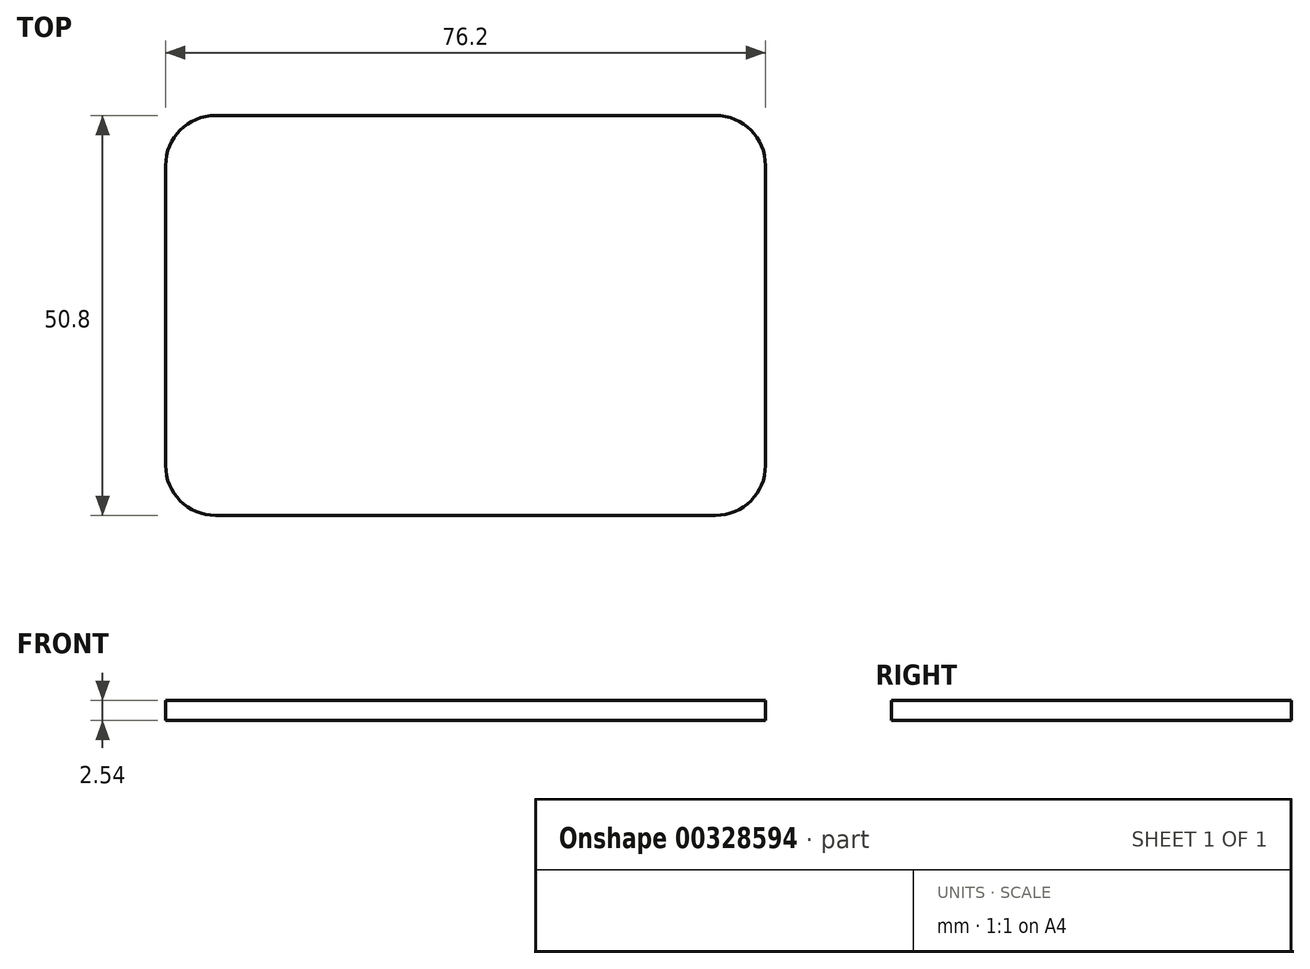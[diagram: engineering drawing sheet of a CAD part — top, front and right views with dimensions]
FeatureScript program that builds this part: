
annotation { "Feature Type Name" : "Feature", "Feature Type Description" : "" }
export const myFeature = defineFeature(function(context is Context, id is Id, definition is map)
    precondition{}
    {
        {
            var Q0;
            Q0=qCreatedBy(makeId("Top.planeOp"),FACE);
            var sketch = newSketch(context, id + "F0", { "sketchPlane" : qUnion([Q0])});
            skLineSegment(sketch, "E0.bottom", {"start": v(-31.75, 25.4) * mm, "end": v(31.75, 25.4) * mm});
            skLineSegment(sketch, "E0.top", {"start": v(-31.75, -25.4) * mm, "end": v(31.75, -25.4) * mm});
            skLineSegment(sketch, "E0.left", {"start": v(-38.1, 19.05) * mm, "end": v(-38.1, -19.05) * mm});
            skLineSegment(sketch, "E0.right", {"start": v(38.1, 19.05) * mm, "end": v(38.1, -19.05) * mm});
            skPoint(sketch, "E0.middle", {"position": v(0, 0) * mm});
            skPoint(sketch, "E1.visualSharp", {"position": v(-38.1, 25.4) * mm});
            skArc(sketch, "E1.filletArc", {"start": v(-31.75, 25.4) * mm, "mid": v(-36.24, 23.54) * mm, "end": v(-38.1, 19.05) * mm});
            skPoint(sketch, "E2.visualSharp", {"position": v(-38.1, -25.4) * mm});
            skArc(sketch, "E2.filletArc", {"start": v(-38.1, -19.05) * mm, "mid": v(-36.24, -23.54) * mm, "end": v(-31.75, -25.4) * mm});
            skPoint(sketch, "E3.visualSharp", {"position": v(38.1, -25.4) * mm});
            skArc(sketch, "E3.filletArc", {"start": v(31.75, -25.4) * mm, "mid": v(36.24, -23.54) * mm, "end": v(38.1, -19.05) * mm});
            skPoint(sketch, "E4.visualSharp", {"position": v(38.1, 25.4) * mm});
            skArc(sketch, "E4.filletArc", {"start": v(38.1, 19.05) * mm, "mid": v(36.24, 23.54) * mm, "end": v(31.75, 25.4) * mm});
            skSolve(sketch);
        }
        {
            var Q0;
            Q0 = qSketchRegion(id + "F0", true);
            extrude(context, id + "F1", {"entities" : qUnion([Q0]), "depth" : 2.54 * mm});
        }
    });
